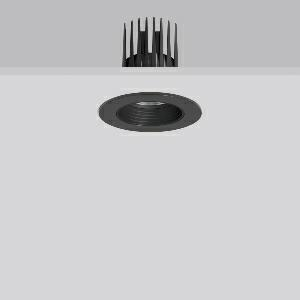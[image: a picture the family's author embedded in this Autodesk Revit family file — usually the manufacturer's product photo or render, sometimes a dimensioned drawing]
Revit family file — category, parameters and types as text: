
# Revit family: heledon_mini_e_901745_003_3_39c0
name_source: partatom
category: Lighting Fixtures
units: mm (PartAtom-declared; Revit-internal decimal feet)

## family parameters
Cut with Voids When Loaded = No
Host = Face
Light Source = No
Part Type = Normal
Room Calculation Point = No
Round Connector Dimension = Use Diameter
Shared = No

## types (1)
- HELEDON mini E (1 x LED Modul 935, 2000 lm, 3500)
    Apparent Load = 20 VA
    Approval mark = CE
    CIE Flux Codes = 98 100 100 100 100
    Color Rendering = 92
    Color Temperature = 3500
    Default Elevation = 1800 mm
    Description = Series: HELEDON mini
Round recessed downlight. Housing: die-cast aluminium, powder-coated. Black plastic ring and recessed LED to prevent glare from the side. Optical assembly with lens made of plastic (polycarbonate) for the best homogeneous light distribution - can be changed without tools. Best colour rendering index Ra>90. Suitable for Recessed ceiling mounting. Installation without tools thanks to spring fastening system. Including separate LED converter with connecting cable 600 mm.High quality converter without flickering and stroboscopic effect. Through-wiring box (5 pole) available as accessory. The following accessories can be mounted without use of tools: interchangeable lenses, decorative glasses, honeycomb louvre, clear and frosted diffusers, white interchangeable plastic ring. 
Colour: deep black, matt (RAL 9005)
Diameter: 124 mm
Height: 3 mm
Cut-out diameter: 114 mm
Recess height: 170 mm
Luminaire: recess height: 120 mm
Lamp: LED
Socket: without socket
Colour temperature: 3500K
Colour rendering index (CRI): 92
System power: 20 W
Rated luminous flux: 2000 lm
Luminous efficiency: 100 lm/W
Control gear: Regulated power supply
Protection class: II
Type of protection: IP 20
    Height = 0 mm  [stored 0 ft]
    Lamp = 1 x LED Modul 935
    Lamp Light Flux = 2000 lm
    Lamp count = 1
    Length = 124 mm  [stored 0.406824 ft]
    Lifetime = 50000 h
    Luminous efficacy = 100 lm/W
    Manufacturer = RZB
    ModVariant = No
    Model = 901745.003.3
    Mounting Place = Ceiling
    Mounting Type = Recessed
    Number of Poles = 1
    OnlyDefault = Yes
    Power Factor = 1
    Product Name = HELEDON mini E
    Product group = Recessed downlights
    ProductGroupID = 402
    Protection Class = Protection class II
    Protection Degree = IP 20
    RLX_Detail_Level = 1
    RLX_Emergency_Light_Flux = 0 lm
    RLX_Emergency_Type = 0
    RLX_Emergency_Type_DB = No
    RlxData = <blob elided: 125077 chars, md5=9a0a0555>
    Socket = socket
    Standby Power = 0 W
    System Light Flux = 2000 lm
    System Power = 20 W
    Type Comments = Product without accessories
    Type Image = 901656.003.jpg
    URL = http://relux.com
    VarID = ---
    Voltage = 230 V
    Voltage Range = 220-240 V
    Weight = 0.00 kg
    Width = 0 mm  [stored 0 ft]

note: [stored X ft] marks values corroborated as IEEE doubles in the binary element streams (Revit-internal decimal feet)

## geometry (parser evidence)
native form markers: Blend x4, Sweep x11
no freeform markers — native parametric forms only
